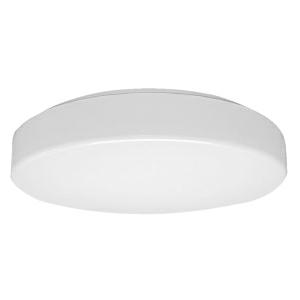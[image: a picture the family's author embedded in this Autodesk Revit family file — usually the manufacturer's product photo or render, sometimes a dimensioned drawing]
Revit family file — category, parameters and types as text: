
# Revit family: oblo_fit_-_oba_4000_830_d_00813354_8649
name_source: partatom
category: Lighting Fixtures
units: mm (PartAtom-declared; Revit-internal decimal feet)

## family parameters
Cut with Voids When Loaded = No
Host = Face
Light Source = No
Part Type = Normal
Room Calculation Point = No
Round Connector Dimension = Use Diameter
Shared = No

## types (1)
- deko (1 x LED, 3350 lm, 3000K)
    Apparent Load = 44 VA
    Approval mark = CE
    CIE Flux Codes = 47 78 95 100 100
    Color Rendering = 80-89
    Color Temperature = 3000K
    Control Gear = Electronic ballast
    Default Elevation = 1800 mm
    Description = OBA 4000/830/D|Surface-mounted luminaire.|light source:   Warm white   |work equipment: Power supply unit|luminous flux: 4300 lm|light distribution: Direct|class of protection: I|technology: Continuously dimmable|mains lead: Direct power supply|glare control: without|special features: DALI Load 1x|
    Frequency = 50 Hz, 60 Hz
    Height = 95 mm
    Lamp = 1 x LED
    Lamp Light Flux = 3350 lm
    Lamp count = 1
    Length = 460 mm
    Luminous efficacy = 76 lm/W
    Manufacturer = Waldmann
    ModVariant = No
    Model = 00813354
    Mounting Place = Ceiling
    Mounting Type = Surface mounted
    Number of Poles = 1
    OnlyDefault = Yes
    Power Factor = 1
    Product Name = OBLO.fit - OBA 4000/830/D
    Product group = Ceiling mounted luminaire
    ProductGroupID = 3
    Protection Class = Protection class I
    Protection Degree = IP 40
    RLX_Detail_Level = 1
    RLX_Emergency_Light_Flux = 0 lm
    RLX_Emergency_Type = 0
    RLX_Emergency_Type_DB = No
    RlxData = <blob elided: 23661 chars, md5=ebf6d13f>
    Socket = socket
    Standby Power = 0 W
    System Light Flux = 3350 lm
    System Power = 44 W
    Type Comments = mit Deko-Ring
    Type Image = oblo_led.jpg
    URL = http://relux.com
    VarID = deko
    Voltage = 230 V
    Voltage Range = 220-240 V
    Weight = 0.00 kg
    Width = 0 mm  [stored 0 ft]

note: [stored X ft] marks values corroborated as IEEE doubles in the binary element streams (Revit-internal decimal feet)

## geometry (parser evidence)
native form markers: Blend x4, Sweep x9
no freeform markers — native parametric forms only
